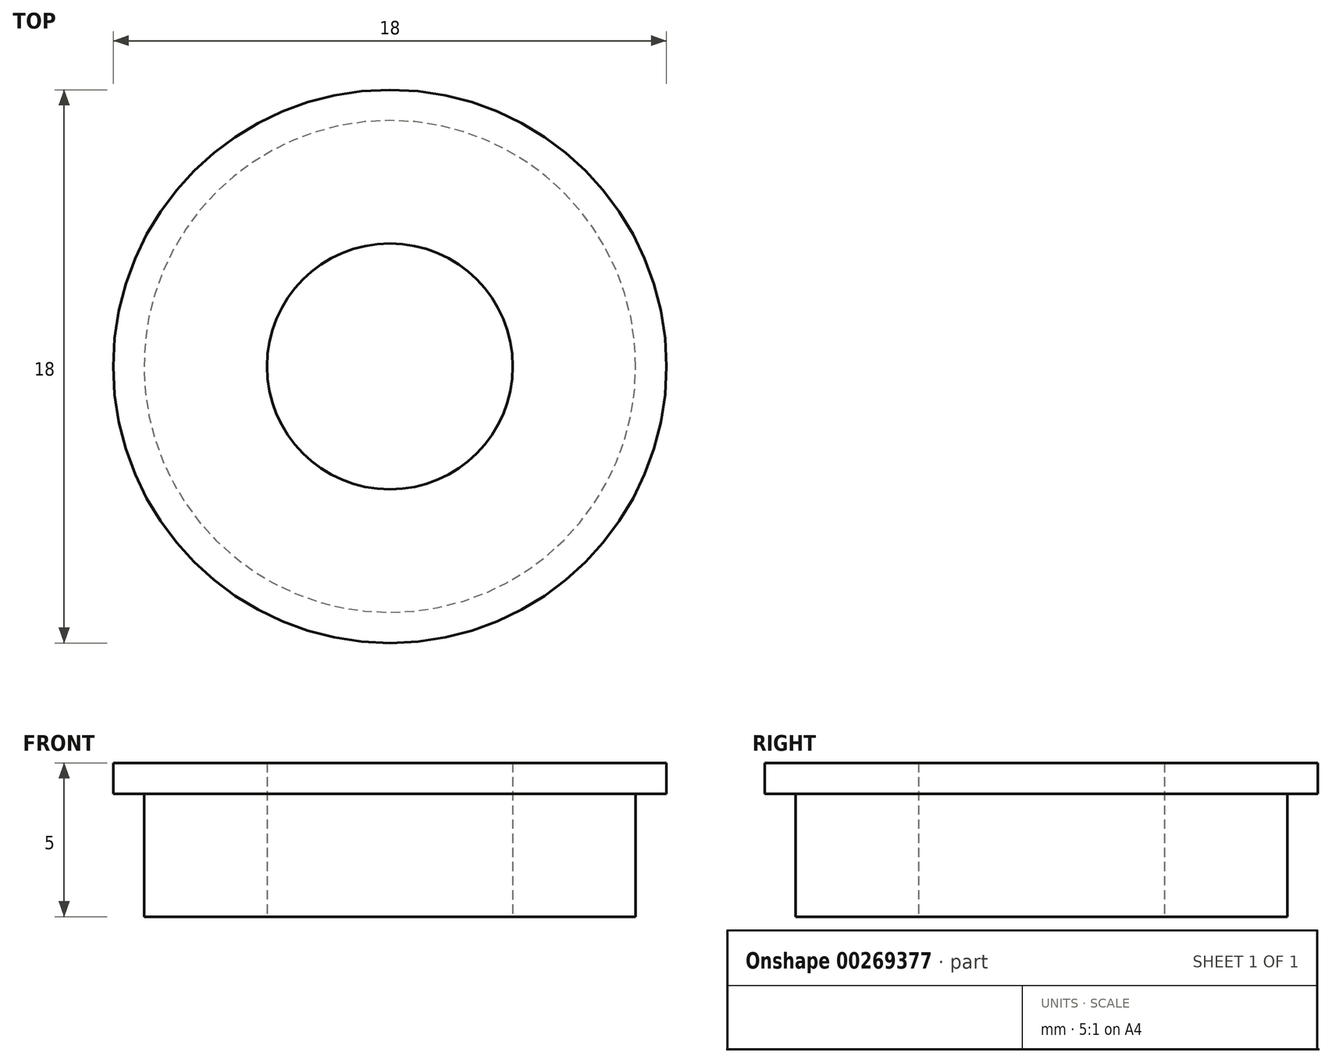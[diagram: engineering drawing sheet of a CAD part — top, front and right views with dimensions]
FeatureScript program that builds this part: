
annotation { "Feature Type Name" : "Feature", "Feature Type Description" : "" }
export const myFeature = defineFeature(function(context is Context, id is Id, definition is map)
    precondition{}
    {
        {
            var Q0;
            Q0=qCreatedBy(makeId("Top.planeOp"),FACE);
            var sketch = newSketch(context, id + "F0", { "sketchPlane" : qUnion([Q0])});
            skCircle(sketch, "E0", {"center": v(0, 0) * mm, "radius": 4 * mm});
            skCircle(sketch, "E1", {"center": v(0, 0) * mm, "radius": 8 * mm});
            skSolve(sketch);
        }
        {
            var Q0;
            Q0=makeQuery(id+"F0.imprint","IMPRINT",FACE,{"disambiguationData":[TD([[makeQuery(id+"F0.imprint","IMPRINT",EDGE,{"derivedFrom":sQuery(id+"F0.wireOp",EDGE,"E0")}),-1.0]])]});
            extrude(context, id + "F1", {"entities" : qUnion([Q0]), "depth" : 5 * mm});
        }
        {
            var Q0;
            Q0=makeQuery(id+"F1.opExtrude","CAP_FACE",FACE,{"disambiguationData":[OSD([sQuery(id+"F0.wireOp",EDGE,"E0"),sQuery(id+"F0.wireOp",EDGE,"E1")])],"isStart":false});
            var sketch = newSketch(context, id + "F2", { "sketchPlane" : qUnion([Q0])});
            skCircle(sketch, "E2", {"center": v(0, 0) * mm, "radius": 9 * mm});
            skCircle(sketch, "E3.0", {"center": v(0, 0) * mm, "radius": 4 * mm});
            skSolve(sketch);
        }
        {
            var Q0;
            Q0 = qSketchRegion(id + "F2", true);
            extrude(context, id + "F3", {"entities" : qUnion([Q0]), "operationType" : NewBodyOperationType.ADD, "oppositeDirection" : true, "depth" : 1 * mm});
        }
    });
